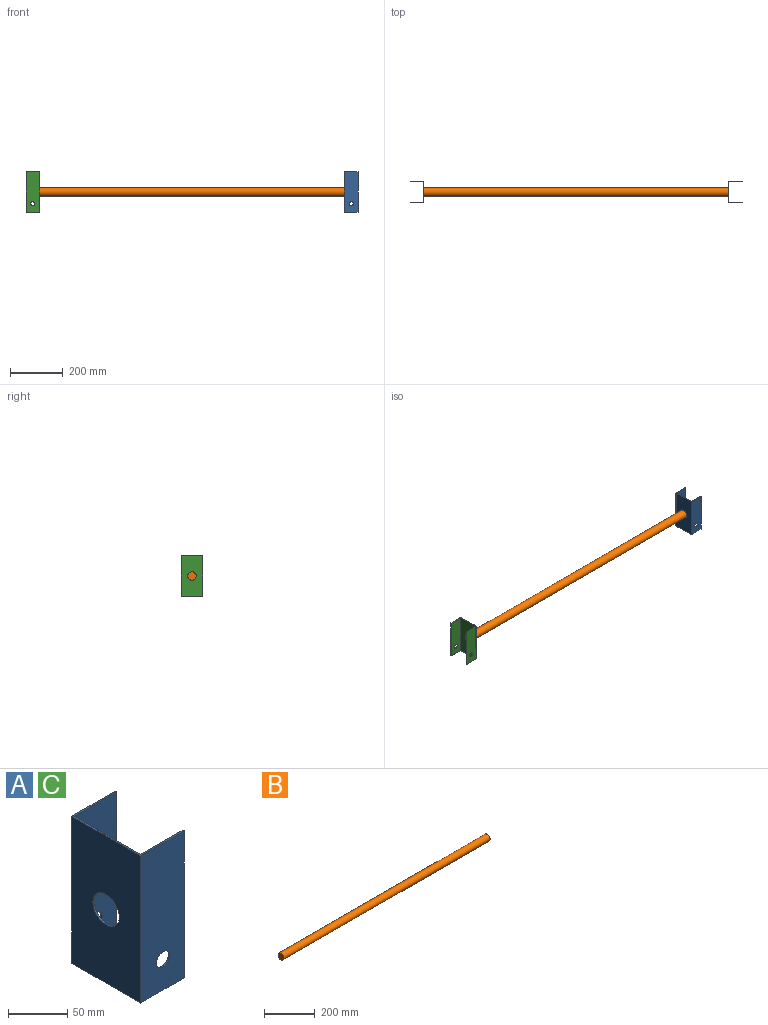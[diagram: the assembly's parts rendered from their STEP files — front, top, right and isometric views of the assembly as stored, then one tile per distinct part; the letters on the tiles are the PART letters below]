
ASSEMBLY  parts=3 mates=5
PART A: 13 faces, bbox 52.4x82.6x152.4 mm
  f0: plane 152.4x1.59mm, normal (1,0,0), area 241.9mm2, adj f1,f7,f8,f9
  f1: plane 152.4x52.39mm, normal (0,1,0), area 7785.9mm2, adj f0,f2,f8,f9,f11
  f2: plane 152.4x82.55mm, normal (-1,0,0), area 11788.9mm2, adj f1,f3,f8,f9,f10
  f3: plane 152.4x52.39mm, normal (0,-1,0), area 7785.9mm2, adj f2,f4,f8,f9,f12
  f4: plane 152.4x1.59mm, normal (1,0,0), area 241.9mm2, adj f3,f5,f8,f9
  f5: plane 152.4x50.8mm, normal (0,1,0), area 7544mm2, adj f4,f6,f8,f9,f12
  f6: plane 152.4x79.38mm, normal (1,0,0), area 11305mm2, adj f5,f7,f8,f9,f10
  f7: plane 152.4x50.8mm, normal (0,-1,0), area 7544mm2, adj f0,f6,f8,f9,f11
  f8: plane 82.55x52.39mm, normal (0,0,1), area 292.3mm2, adj f0,f1,f2,f3,f4,f5,f6,f7
  f9: plane 82.55x52.39mm, normal (0,0,-1), area 292.3mm2, adj f0,f1,f2,f3,f4,f5,f6,f7
  f10: cylinder r=15.88mm len=31.75mm, axis (-1,0,0), area 158.3mm2, adj f2,f6
  f11: cylinder r=7.94mm len=15.88mm, axis (0,-1,0), area 79.2mm2, adj f1,f7
  f12: cylinder r=7.94mm len=15.88mm, axis (0,-1,0), area 79.2mm2, adj f3,f5
PART B: 3 faces, bbox 1155.7x31.8x31.8 mm
  f0: cylinder r=15.88mm len=1155.7mm, axis (1,0,0), area 115276mm2, adj f1,f2
  f1: plane 31.75x31.75mm, normal (-1,0,0), area 791.7mm2, adj f0
  f2: plane 31.75x31.75mm, normal (1,0,0), area 791.7mm2, adj f0
PART C: same geometry as A
PLACE A at identity fixed
PLACE B t=(0,39.69,76.2)mm
PLACE C rot(axis=(0,0,1),180deg) t=(-1155.7,79.38,0)mm
MATE fastened B.f0 <-> C.f10  axis (-1,0,0) through (-1155.7,39.69,76.2)mm
MATE slider C.f10 <-> B.f0  axis (1,0,0) through (-1154.11,39.69,76.2)mm
MATE fastened B.f0 <-> A.f10  axis (1,0,0) through (0,39.69,76.2)mm
MATE slider B.f0 <-> A.f10  axis (1,0,0) through (0,39.69,76.2)mm
MATE parallel C.f2 <-> A.f2  axis (1,0,0) through (-1154.11,39.69,0)mm
